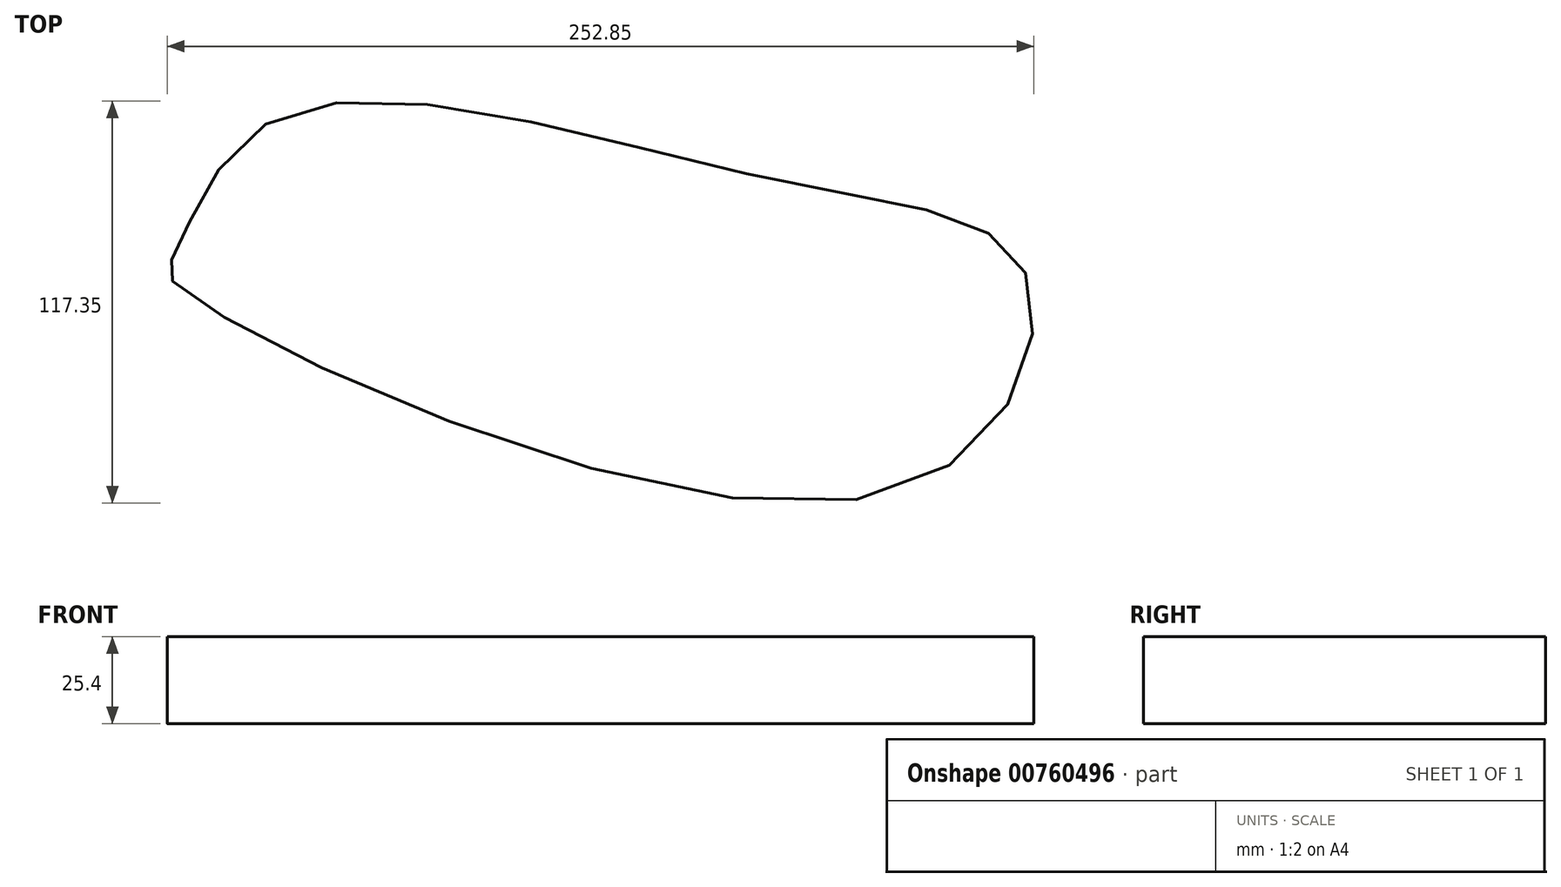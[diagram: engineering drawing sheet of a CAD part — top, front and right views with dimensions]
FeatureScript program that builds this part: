
annotation { "Feature Type Name" : "Feature", "Feature Type Description" : "" }
export const myFeature = defineFeature(function(context is Context, id is Id, definition is map)
    precondition{}
    {
        {
            var Q0;
            Q0=qCreatedBy(makeId("Top.planeOp"),FACE);
            var sketch = newSketch(context, id + "F0", { "sketchPlane" : qUnion([Q0])});
            skFitSpline(sketch, "E0", {"points": [v(-132.63, 21.18) * mm, v(-132.19, 28.76) * mm, v(-102.76, 68.43) * mm, v(43.91, 50.6) * mm, v(116.58, 22.96) * mm, v(74.23, -41.24) * mm, v(-132.63, 21.18) * mm]});
            skSolve(sketch);
        }
        {
            var Q0;
            Q0=makeQuery(id+"F0.imprint","IMPRINT",FACE,{"disambiguationData":[TD([[makeQuery(id+"F0.imprint","IMPRINT",EDGE,{"derivedFrom":sQuery(id+"F0.wireOp",EDGE,"E0")}),-1.0]])]});
            extrude(context, id + "F1", {"entities" : qUnion([Q0]), "depth" : 25.4 * mm, "offsetDistance" : 25.4 * mm});
        }
    });
